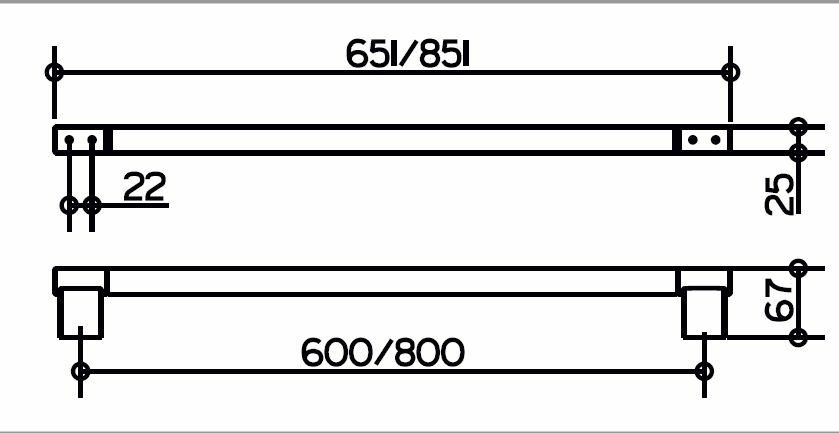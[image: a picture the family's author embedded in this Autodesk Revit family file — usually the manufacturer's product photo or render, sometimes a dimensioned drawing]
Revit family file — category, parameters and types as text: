
# Revit family: KEUCO_04988070000_
name_source: partatom
category: Generic Models
revit_build: Autodesk Revit 2016 (Build: 20150220_1215(x64)
units: mm (PartAtom-declared; Revit-internal decimal feet)

## family parameters
Always vertical = Yes
Can host rebar = No
Cut with Voids When Loaded = No
Part Type = Normal
Room Calculation Point = No
Round Connector Dimension = Use Diameter
Shared = No
Work Plane-Based = No

## types (3) — shared parameters
Gewicht = 1.72
Kategorie = ACC
Manufacturer = KEUCO
Preisgruppe = 1
Serie = Plan
URL = https://www.keuco.com
Verwendung = GWC / WP

## per-type parameters (varying)
| type | Ausschreibungstext | Description | Material Abdeckung | Material Eimer |
| 04988070000 | KEUCO Abfalleimer 04988070000
Abfalleimer aus hochwertigem Edelstahl als Standmodel mit Deckel und Tretpedal
komplett mit herausnehmbaren Kunststoff-Einsatz, für leichtes reinigen, 
5 l Fassungsvermögen
Höhe 298 mm, Durchmesser 200 mm, 
Tiefe (ohne Tretpedal) 240 mm | mit herausnehmbarem schwarzen Innenbehälter
Fassungsvermögen: 5 l | Edelstahl | Edelstahl |
| 04988010000 | KEUCO Abfalleimer 04988010000
Abfalleimer in Chrom-finish (Edelstahl poliert) 
als Standmodell mit Deckel und Tretpedal,
komplett mit herausnehmbaren Kunststoff-Einsatz, für leichtes reinigen, 
5 l Fassungsvermögen
Höhe 298 mm, Durchmesser 200 mm, 
Tiefe (ohne Tretpedal) 240 mm | mit herausnehmbarem schwarzem Innenbehälter
Fassungsvermögen: 5 l | Chrom-finish (Edelstahl poliert) | Chrom-finish (Edelstahl poliert) |
| 04988170000 | KEUCO Abfalleimer 04988170000
Aluminium silber-eloxierter Abfalleimer als Standmodell mit Deckel und Tretpedal
komplett mit herausnehmbaren Kunststoff-Einsatz, für leichtes reinigen, 
5 l Fassungsvermögen
Höhe 298 mm, Durchmesser 200 mm, 
Tiefe (ohne Tretpedal) 240 mm | mit herausnehmbarem schwarzem Innenbehälter
Fassungsvermögen: 5 l | Aluminium-finish | Aluminium-finish |

note: column(s) folded — value = type name in every type: Artikelnummer

## geometry (parser evidence)
native form markers: Sweep x3
no freeform markers — native parametric forms only
